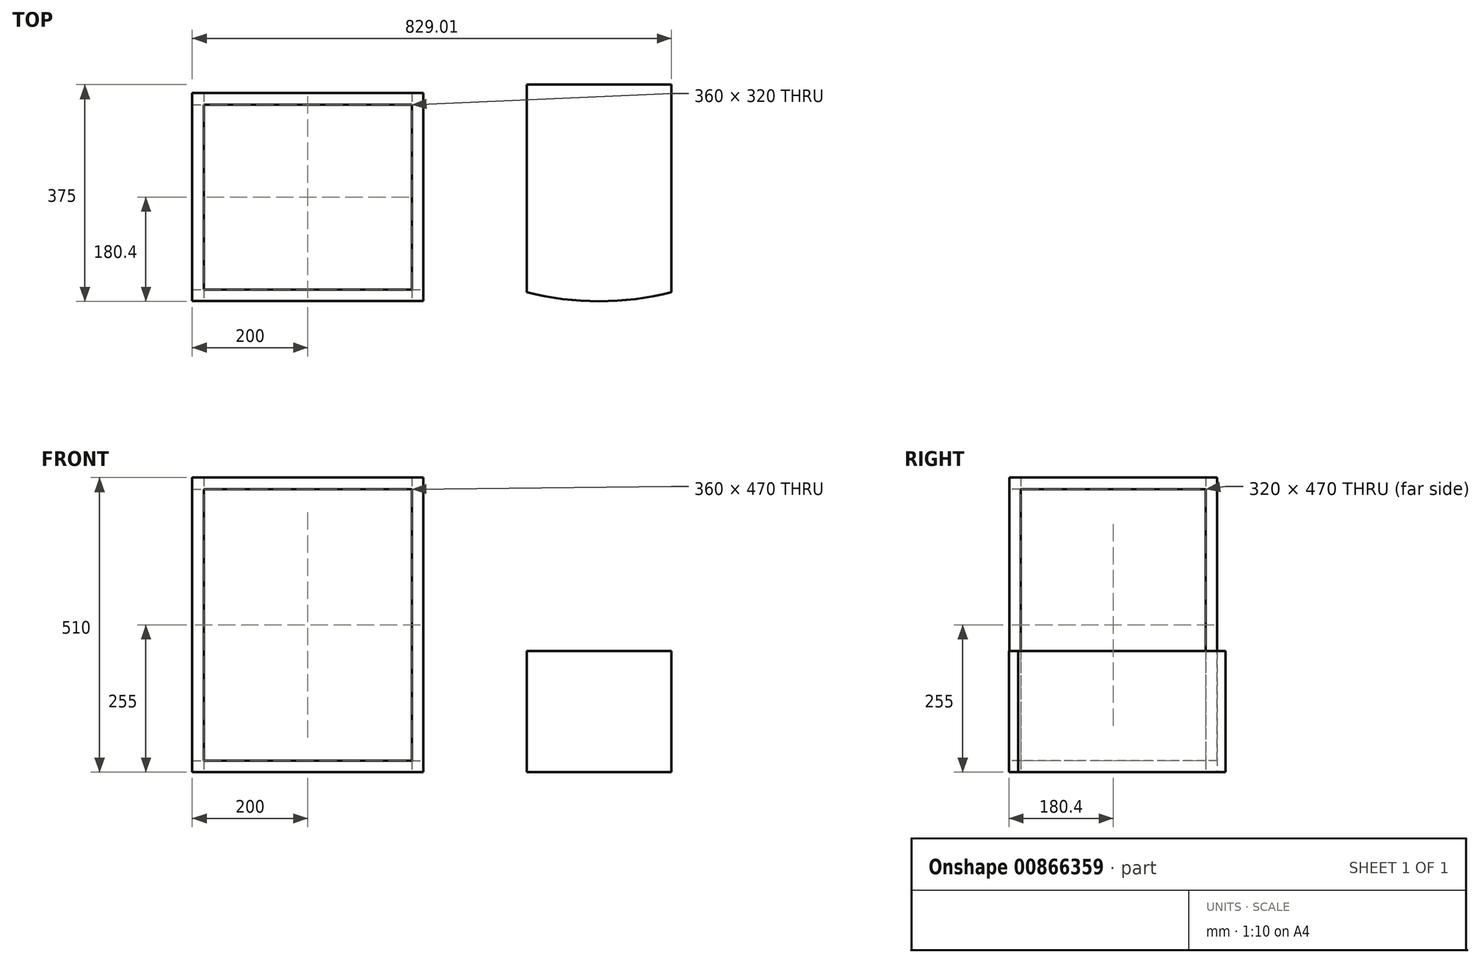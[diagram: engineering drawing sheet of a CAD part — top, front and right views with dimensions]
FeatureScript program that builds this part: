
annotation { "Feature Type Name" : "Feature", "Feature Type Description" : "" }
export const myFeature = defineFeature(function(context is Context, id is Id, definition is map)
    precondition{}
    {
        {
            var Q0;
            Q0=qCreatedBy(makeId("Top.planeOp"),FACE);
            var sketch = newSketch(context, id + "F0", { "sketchPlane" : qUnion([Q0])});
            skLineSegment(sketch, "E0.bottom", {"start": v(-200, 180) * mm, "end": v(200, 180) * mm});
            skLineSegment(sketch, "E0.top", {"start": v(-200, -180) * mm, "end": v(200, -180) * mm});
            skLineSegment(sketch, "E0.left", {"start": v(-200, 180) * mm, "end": v(-200, -180) * mm});
            skLineSegment(sketch, "E0.right", {"start": v(200, 180) * mm, "end": v(200, -180) * mm});
            skLineSegment(sketch, "E1.0", {"start": v(-180, 160) * mm, "end": v(180, 160) * mm});
            skLineSegment(sketch, "E1.1", {"start": v(-180, 160) * mm, "end": v(-180, -160) * mm});
            skLineSegment(sketch, "E1.2", {"start": v(-180, -160) * mm, "end": v(180, -160) * mm});
            skLineSegment(sketch, "E1.3", {"start": v(180, 160) * mm, "end": v(180, -160) * mm});
            skLineSegment(sketch, "E2", {"start": v(180, 0) * mm, "end": v(-180, 0) * mm, "construction": true});
            skLineSegment(sketch, "E3", {"start": v(0, 160) * mm, "end": v(0, -160) * mm, "construction": true});
            skLineSegment(sketch, "E4.bottom", {"start": v(379.01, 194.6) * mm, "end": v(629.01, 194.6) * mm});
            skLineSegment(sketch, "E4.top", {"start": v(379.01, -164.52) * mm, "end": v(629.01, -164.52) * mm});
            skLineSegment(sketch, "E4.left", {"start": v(379.01, 194.6) * mm, "end": v(379.01, -164.52) * mm});
            skLineSegment(sketch, "E4.right", {"start": v(629.01, 194.6) * mm, "end": v(629.01, -164.52) * mm});
            skArc(sketch, "E5", {"start": v(379.01, -164.52) * mm, "mid": v(504.01, -180.4) * mm, "end": v(629.01, -164.52) * mm});
            skSolve(sketch);
        }
        {
            var Q0;
            Q0=makeQuery(id+"F0.imprint","IMPRINT",FACE,{"disambiguationData":[TD([[makeQuery(id+"F0.imprint","IMPRINT",EDGE,{"derivedFrom":sQuery(id+"F0.wireOp",EDGE,"E0.bottom")}),-1.0]])]});
            extrude(context, id + "F1", {"entities" : qUnion([Q0]), "depth" : 510 * mm, "offsetDistance" : 25 * mm});
        }
        {
            var Q0;
            Q0=makeQuery(id+"F1.opExtrude","SWEPT_FACE",FACE,{"disambiguationData":[OSD([sQuery(id+"F0.wireOp",EDGE,"E0.top")])]});
            var sketch = newSketch(context, id + "F2", { "sketchPlane" : qUnion([Q0])});
            skLineSegment(sketch, "E6.0", {"start": v(-180, 490) * mm, "end": v(180, 490) * mm});
            skLineSegment(sketch, "E6.1", {"start": v(-180, 490) * mm, "end": v(-180, 20) * mm});
            skLineSegment(sketch, "E6.2", {"start": v(-180, 20) * mm, "end": v(180, 20) * mm});
            skLineSegment(sketch, "E6.3", {"start": v(180, 490) * mm, "end": v(180, 20) * mm});
            skSolve(sketch);
        }
        {
            var Q0;
            Q0=makeQuery(id+"F2.imprint","IMPRINT",FACE,{"disambiguationData":[TD([[makeQuery(id+"F2.imprint","IMPRINT",EDGE,{"derivedFrom":sQuery(id+"F2.wireOp",EDGE,"E6.0")}),-1.0]])]});
            extrude(context, id + "F3", {"entities" : qUnion([Q0]), "operationType" : NewBodyOperationType.REMOVE, "oppositeDirection" : true, "depth" : 638.1 * mm, "offsetDistance" : 25 * mm});
        }
        {
            var Q0;
            Q0=makeQuery(id+"F1.opExtrude","SWEPT_FACE",FACE,{"disambiguationData":[OSD([sQuery(id+"F0.wireOp",EDGE,"E0.right")])]});
            var sketch = newSketch(context, id + "F4", { "sketchPlane" : qUnion([Q0])});
            skLineSegment(sketch, "E7.0", {"start": v(-160, 490) * mm, "end": v(-160, 20) * mm});
            skLineSegment(sketch, "E7.1", {"start": v(160, 490) * mm, "end": v(-160, 490) * mm});
            skLineSegment(sketch, "E7.2", {"start": v(160, 490) * mm, "end": v(160, 20) * mm});
            skLineSegment(sketch, "E7.3", {"start": v(160, 20) * mm, "end": v(-160, 20) * mm});
            skSolve(sketch);
        }
        {
            var Q0;
            Q0=makeQuery(id+"F4.imprint","IMPRINT",FACE,{"disambiguationData":[TD([[makeQuery(id+"F4.imprint","IMPRINT",EDGE,{"derivedFrom":sQuery(id+"F4.wireOp",EDGE,"E7.0")}),1.0]])]});
            extrude(context, id + "F5", {"entities" : qUnion([Q0]), "operationType" : NewBodyOperationType.REMOVE, "oppositeDirection" : true, "depth" : 520 * mm, "offsetDistance" : 25 * mm});
        }
        {
            var Q0;
            Q0=makeQuery(id+"F0.imprint","IMPRINT",FACE,{"disambiguationData":[TD([[makeQuery(id+"F0.imprint","IMPRINT",EDGE,{"derivedFrom":sQuery(id+"F0.wireOp",EDGE,"E4.top")}),-1.0]])]});
            var Q1;
            Q1=makeQuery(id+"F0.imprint","IMPRINT",FACE,{"disambiguationData":[TD([[makeQuery(id+"F0.imprint","IMPRINT",EDGE,{"derivedFrom":sQuery(id+"F0.wireOp",EDGE,"E4.bottom")}),-1.0]])]});
            extrude(context, id + "F6", {"entities" : qUnion([Q0, Q1]), "depth" : 210 * mm, "offsetDistance" : 25 * mm});
        }
    });
